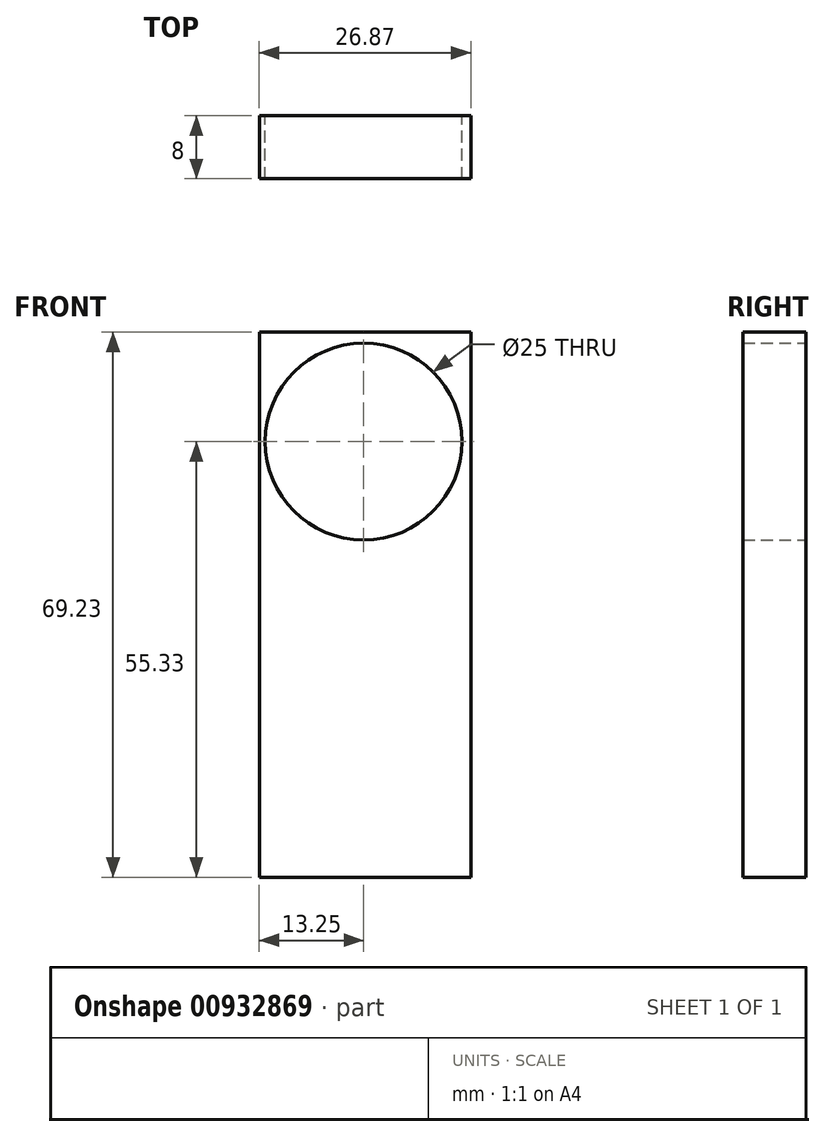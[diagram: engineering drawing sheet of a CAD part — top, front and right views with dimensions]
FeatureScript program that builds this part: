
annotation { "Feature Type Name" : "Feature", "Feature Type Description" : "" }
export const myFeature = defineFeature(function(context is Context, id is Id, definition is map)
    precondition{}
    {
        {
            var Q0;
            Q0=qCreatedBy(makeId("Front.planeOp"),FACE);
            var sketch = newSketch(context, id + "F0", { "sketchPlane" : qUnion([Q0])});
            skCircle(sketch, "E0", {"center": v(0, 0) * mm, "radius": 12.5 * mm});
            skLineSegment(sketch, "E1.bottom", {"start": v(-13.25, 13.9) * mm, "end": v(13.62, 13.9) * mm});
            skLineSegment(sketch, "E1.top", {"start": v(-13.25, -55.33) * mm, "end": v(13.62, -55.33) * mm});
            skLineSegment(sketch, "E1.left", {"start": v(-13.25, 13.9) * mm, "end": v(-13.25, -55.33) * mm});
            skLineSegment(sketch, "E1.right", {"start": v(13.62, 13.9) * mm, "end": v(13.62, -55.33) * mm});
            skSolve(sketch);
        }
        {
            var Q0;
            Q0=makeQuery(id+"F0.imprint","IMPRINT",FACE,{"disambiguationData":[TD([[makeQuery(id+"F0.imprint","IMPRINT",EDGE,{"derivedFrom":sQuery(id+"F0.wireOp",EDGE,"E0")}),-1.0]])]});
            extrude(context, id + "F1", {"entities" : qUnion([Q0]), "depth" : 8 * mm, "offsetDistance" : 25 * mm});
        }
    });
